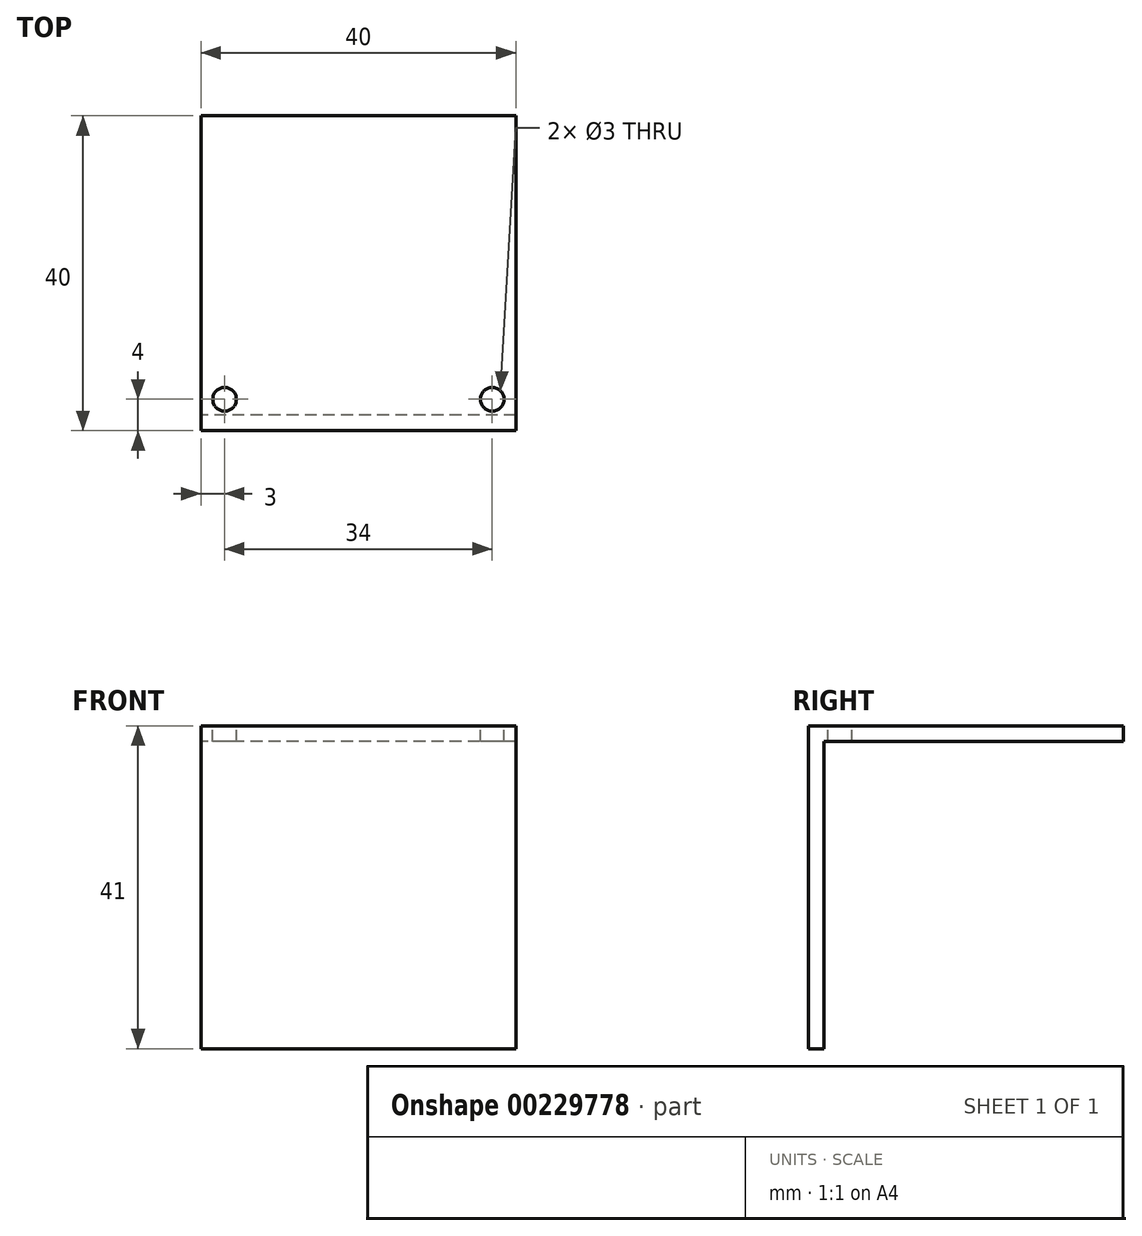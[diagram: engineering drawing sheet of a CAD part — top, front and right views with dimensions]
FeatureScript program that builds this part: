
annotation { "Feature Type Name" : "Feature", "Feature Type Description" : "" }
export const myFeature = defineFeature(function(context is Context, id is Id, definition is map)
    precondition{}
    {
        {
            var Q0;
            Q0=qCreatedBy(makeId("Top.planeOp"),FACE);
            var sketch = newSketch(context, id + "F0", { "sketchPlane" : qUnion([Q0])});
            skLineSegment(sketch, "E0.bottom", {"start": v(20, 20) * mm, "end": v(-20, 20) * mm});
            skLineSegment(sketch, "E0.top", {"start": v(20, -20) * mm, "end": v(-20, -20) * mm});
            skLineSegment(sketch, "E0.left", {"start": v(20, 20) * mm, "end": v(20, -20) * mm});
            skLineSegment(sketch, "E0.right", {"start": v(-20, 20) * mm, "end": v(-20, -20) * mm});
            skPoint(sketch, "E0.middle", {"position": v(0, 0) * mm});
            skSolve(sketch);
        }
        {
            var Q0;
            Q0 = qSketchRegion(id + "F0", true);
            extrude(context, id + "F1", {"entities" : qUnion([Q0]), "depth" : 2 * mm, "offsetDistance" : 25 * mm});
        }
        {
            var Q0;
            Q0=qCreatedBy(makeId("Right.planeOp"),FACE);
            var sketch = newSketch(context, id + "F2", { "sketchPlane" : qUnion([Q0])});
            skLineSegment(sketch, "E1.bottom", {"start": v(-18, 0) * mm, "end": v(-20, 0) * mm});
            skLineSegment(sketch, "E1.top", {"start": v(-18, -39) * mm, "end": v(-20, -39) * mm});
            skLineSegment(sketch, "E1.left", {"start": v(-18, 0) * mm, "end": v(-18, -39) * mm});
            skLineSegment(sketch, "E1.right", {"start": v(-20, 0) * mm, "end": v(-20, -39) * mm});
            skSolve(sketch);
        }
        {
            var Q0;
            Q0 = qSketchRegion(id + "F2", true);
            extrude(context, id + "F3", {"entities" : qUnion([Q0]), "operationType" : NewBodyOperationType.ADD, "depth" : 20 * mm, "offsetDistance" : 25 * mm, "hasSecondDirection" : true, "secondDirectionOppositeDirection" : true, "secondDirectionDepth" : 20 * mm});
        }
        {
            var Q0;
            Q0=makeQuery(id+"F1.opExtrude","CAP_FACE",FACE,{"disambiguationData":[OSD([sQuery(id+"F0.wireOp",EDGE,"E0.bottom"),sQuery(id+"F0.wireOp",EDGE,"E0.top"),sQuery(id+"F0.wireOp",EDGE,"E0.left"),sQuery(id+"F0.wireOp",EDGE,"E0.right")])],"isStart":false});
            var sketch = newSketch(context, id + "F4", { "sketchPlane" : qUnion([Q0])});
            skPoint(sketch, "E2", {"position": v(-17, -16) * mm});
            skPoint(sketch, "E3", {"position": v(17, -16) * mm});
            skSolve(sketch);
        }
        {
            var Q0;
            Q0=sQuery(id+"F4.wireOp",VERTEX,"E2");
            var Q1;
            Q1=sQuery(id+"F4.wireOp",VERTEX,"E3");
            var Q2;
            Q2=makeQuery(id+"F1.opExtrude","SWEPT_BODY",BODY,{"disambiguationData":[OSD([sQuery(id+"F0.wireOp",EDGE,"E0.bottom"),sQuery(id+"F0.wireOp",EDGE,"E0.top"),sQuery(id+"F0.wireOp",EDGE,"E0.left"),sQuery(id+"F0.wireOp",EDGE,"E0.right")])]});
            hole(context, id + "F5", {"style" : HoleStyle.SIMPLE, "endStyle" : HoleEndStyle.THROUGH, "holeDiameter" : 3 * mm, "majorDiameter" : 5 * mm, "isTappedThrough" : true, "tappedDepth" : 12 * mm, "tapClearance" : 3, "locations" : qUnion([Q0, Q1]), "scope" : qUnion([Q2])});
        }
    });
